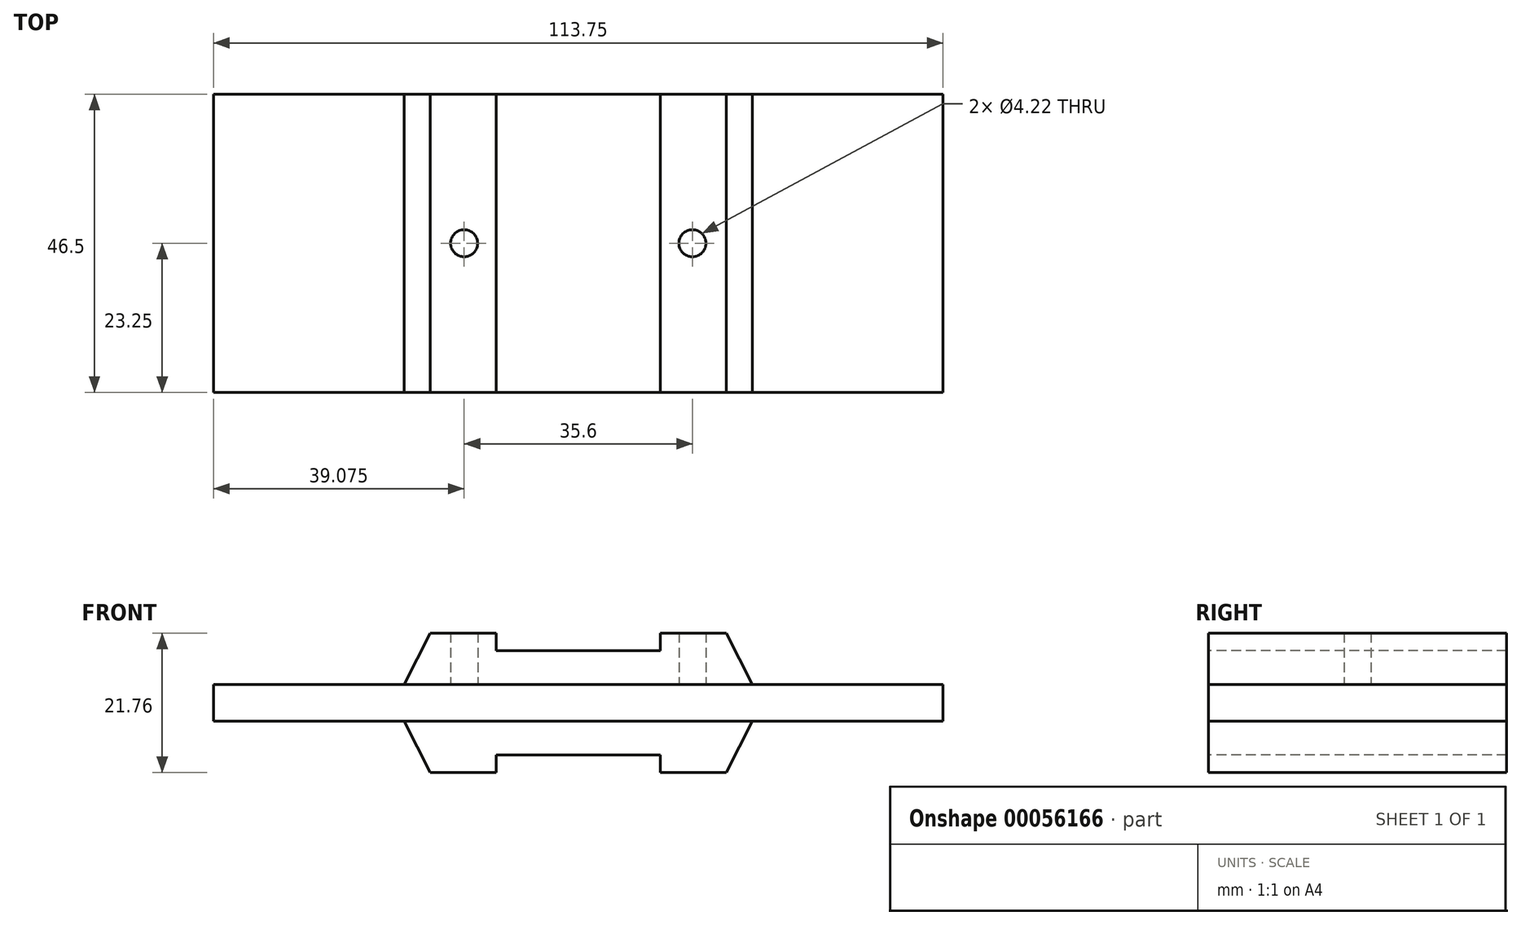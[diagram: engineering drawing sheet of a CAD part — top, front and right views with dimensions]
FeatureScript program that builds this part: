
annotation { "Feature Type Name" : "Feature", "Feature Type Description" : "" }
export const myFeature = defineFeature(function(context is Context, id is Id, definition is map)
    precondition{}
    {
        {
            var Q0;
            Q0=qCreatedBy(makeId("Top.planeOp"),FACE);
            var sketch = newSketch(context, id + "F0", { "sketchPlane" : qUnion([Q0])});
            skLineSegment(sketch, "E0.bottom", {"start": v(0, 0) * mm, "end": v(113.75, 0) * mm});
            skLineSegment(sketch, "E0.top", {"start": v(0, 46.5) * mm, "end": v(113.75, 46.5) * mm});
            skLineSegment(sketch, "E0.left", {"start": v(0, 0) * mm, "end": v(0, 46.5) * mm});
            skLineSegment(sketch, "E0.right", {"start": v(113.75, 0) * mm, "end": v(113.75, 46.5) * mm});
            skSolve(sketch);
        }
        {
            var Q0;
            Q0=makeQuery(id+"F0.imprint","IMPRINT",FACE,{"disambiguationData":[TD([[makeQuery(id+"F0.imprint","IMPRINT",EDGE,{"derivedFrom":sQuery(id+"F0.wireOp",EDGE,"E0.bottom")}),1.0]])]});
            extrude(context, id + "F1", {"entities" : qUnion([Q0]), "endBound" : BoundingType.SYMMETRIC, "depth" : 5.75 * mm});
        }
        {
            var Q0;
            Q0=makeQuery(id+"F1.opExtrude","SWEPT_FACE",FACE,{"disambiguationData":[OSD([sQuery(id+"F0.wireOp",EDGE,"E0.bottom")])]});
            var sketch = newSketch(context, id + "F2", { "sketchPlane" : qUnion([Q0])});
            skLineSegment(sketch, "E1", {"start": v(29.75, 2.87) * mm, "end": v(33.8, 10.88) * mm});
            skLineSegment(sketch, "E2", {"start": v(33.8, 10.88) * mm, "end": v(44.1, 10.88) * mm});
            skLineSegment(sketch, "E3", {"start": v(44.1, 10.88) * mm, "end": v(44.1, 8.1) * mm});
            skLineSegment(sketch, "E4", {"start": v(44.1, 8.1) * mm, "end": v(69.65, 8.1) * mm});
            skLineSegment(sketch, "E5", {"start": v(69.65, 8.1) * mm, "end": v(69.65, 10.88) * mm});
            skLineSegment(sketch, "E6", {"start": v(69.65, 10.88) * mm, "end": v(79.94, 10.88) * mm});
            skLineSegment(sketch, "E7", {"start": v(79.94, 10.87) * mm, "end": v(84, 2.87) * mm});
            skLineSegment(sketch, "E8", {"start": v(84, 2.88) * mm, "end": v(84, -2.88) * mm});
            skLineSegment(sketch, "E9", {"start": v(84, -2.87) * mm, "end": v(79.94, -10.87) * mm});
            skLineSegment(sketch, "E10", {"start": v(79.94, -10.88) * mm, "end": v(69.65, -10.88) * mm});
            skLineSegment(sketch, "E11", {"start": v(69.65, -10.88) * mm, "end": v(69.65, -8.1) * mm});
            skLineSegment(sketch, "E12", {"start": v(69.65, -8.1) * mm, "end": v(44.1, -8.1) * mm});
            skLineSegment(sketch, "E13", {"start": v(44.1, -8.1) * mm, "end": v(44.1, -10.88) * mm});
            skLineSegment(sketch, "E14", {"start": v(44.1, -10.88) * mm, "end": v(33.81, -10.88) * mm});
            skLineSegment(sketch, "E15", {"start": v(33.81, -10.87) * mm, "end": v(29.75, -2.87) * mm});
            skLineSegment(sketch, "E16", {"start": v(29.75, -2.88) * mm, "end": v(29.75, 2.88) * mm});
            skPoint(sketch, "E17.endSnap0", {"position": v(56.87, -8.1) * mm});
            skLineSegment(sketch, "E18", {"start": v(56.88, 8.1) * mm, "end": v(56.88, -8.1) * mm, "construction": true});
            skLineSegment(sketch, "E19", {"start": v(113.75, 0) * mm, "end": v(56.88, 0) * mm, "construction": true});
            skLineSegment(sketch, "E20", {"start": v(0, 0) * mm, "end": v(56.88, 0) * mm, "construction": true});
            skSolve(sketch);
        }
        {
            var Q0;
            {var subQ0=sQuery(id+"F2.wireOp",EDGE,"E9");Q0=makeQuery(id+"F2.imprint","IMPRINT",FACE,{"disambiguationData":[TD([[makeQuery(id+"F2.imprint","IMPRINT",EDGE,{"derivedFrom":subQ0}),-1.0]])]});}
            var Q1;
            {var subQ0=sQuery(id+"F2.wireOp",EDGE,"E1");Q1=makeQuery(id+"F2.imprint","IMPRINT",FACE,{"disambiguationData":[TD([[makeQuery(id+"F2.imprint","IMPRINT",EDGE,{"derivedFrom":subQ0}),-1.0]])]});}
            extrude(context, id + "F3", {"entities" : qUnion([Q0, Q1]), "oppositeDirection" : true, "depth" : 46.5 * mm});
        }
        {
            var Q0;
            Q0=makeQuery(id+"F1.opExtrude","CAP_FACE",FACE,{"disambiguationData":[OSD([sQuery(id+"F0.wireOp",EDGE,"E0.bottom"),sQuery(id+"F0.wireOp",EDGE,"E0.top"),sQuery(id+"F0.wireOp",EDGE,"E0.left"),sQuery(id+"F0.wireOp",EDGE,"E0.right")])],"isStart":false});
            var sketch = newSketch(context, id + "F4", { "sketchPlane" : qUnion([Q0])});
            skCircle(sketch, "E21", {"center": v(39.07, 23.25) * mm, "radius": 2.1 * mm});
            skPoint(sketch, "E21.centerSnap0", {"position": v(0, 23.25) * mm});
            skCircle(sketch, "E22", {"center": v(74.68, 23.25) * mm, "radius": 2.1 * mm});
            skPoint(sketch, "E22.centerSnap0", {"position": v(113.75, 23.25) * mm});
            skLineSegment(sketch, "E23", {"start": v(0, 23.25) * mm, "end": v(39.07, 23.25) * mm, "construction": true});
            skLineSegment(sketch, "E24", {"start": v(113.75, 23.25) * mm, "end": v(74.68, 23.25) * mm, "construction": true});
            skSolve(sketch);
        }
        {
            var Q0;
            Q0 = qSketchRegion(id + "F4", true);
            var Q1;
            Q1=sQuery(id+"F4.wireOp",EDGE,"E21");
            var Q2;
            Q2=sQuery(id+"F4.wireOp",EDGE,"E22");
            var Q3;
            Q3=makeQuery(id+"F3.opExtrude","SWEPT_FACE",FACE,{"disambiguationData":[OSD([sQuery(id+"F2.wireOp",EDGE,"E2")])]});
            extrude(context, id + "F5", {"entities" : qUnion([Q0]), "operationType" : NewBodyOperationType.REMOVE, "surfaceEntities" : qUnion([Q1, Q2]), "endBound" : BoundingType.UP_TO_SURFACE, "endBoundEntityFace" : qUnion([Q3]), "depth" : 25 * mm});
        }
    });
